# Revit family: Kälteschelle ALU-PU 80 -s-, DS 20, M10-M12, Ø108-133
name_source: partatom
category: HLS-Bauteile
revit_build: Autodesk Revit 2017 (Build: 20190507_1515(x64)
units: mm (PartAtom-declared; Revit-internal decimal feet)

## family parameters
Arbeitsebenenbasiert = Ja
Beim Laden mit Abzugskörper schneiden = Nein
Bemaßung runder Anschluss = Durchmesser verwenden
Gemeinsam genutzt = Ja
Immer vertikal = Nein
Raumberechnungspunkt = Nein
Teiletyp = Normal

## types (3) — shared parameters
A = 45 mm
Anschluss = M10/M12
BP = 14 mm  [stored 0.0459318 ft]
Baustoffklasse = B2
DS = 20 mm  [stored 0.0656168 ft]
DVS = 7 mm  [stored 0.0229659 ft]
Dichte Kern = 80 kg/m³
Dichte Mantel = 2.700 kg/m³
Dicke Mantel = 0,08 mm
Dämmkörper = ALU/PU
Dämmstärke = 20 mm  [stored 0.0656168 ft]
Fabrikat = MEFA
Firma = MEFA Befestigungs- und Montagesysteme GmbH
HGA = 22 mm  [stored 0.0721785 ft]
Kurztext1 = Kälteschelle RG80s ALU/PU
L Ü Bogen = 19 mm
MD = 3 mm  [stored 0.00984252 ft]
Material = Stahl
Material Mantel = Alufolie
Mengeneinheit = St
Oberflaeche = galvanisch verzinkt
Vorgabe-Ansicht = 1219 mm
Wasserdampfdiffusionswiderstand = 18750 µ
Wärmeleitfähigkeit = 0.025 W/mK
d1 = 7 mm  [stored 0.0229659 ft]
max. Temperaturbeständigkeit = 120 °C
mittl. Nenndruckfestigkeit Kern = 0,5 N/mm²
stat. Belastung Kern = 0,1 N/mm²
vpe = 1 St

## per-type parameters (varying)
- Kälteschelle ALU-PU 80 -s-, DS 20, M10/M12, Ø108: AB=0 mm  [stored 0 ft]; Anschlußhöhe=45 mm; Artikelnummer=75210850; B=196 mm; Breite=197 mm; D=108 mm; D0=148 mm; DF1=20 mm  [stored 0.0656168 ft]; DF2=20 mm  [stored 0.0656168 ft]; Dmax=110 mm; Dmin=108 mm; EAN=4250928443106; Gewicht=0.45 kg; Gewicht pro Bauteil=0.45 kg; H=176 mm; Kurztext2=108 mm Iso 20 x 83 mm M10/M12; L=83 mm  [stored 0.27231 ft]; MB=25 mm  [stored 0.082021 ft]; Materialname=DD11; R=74 mm; RM=77 mm; Rohraußendurchmesser Stahl=108 mm; Rohrschellentyp=Omnia MB; S=176 mm; S1=167 mm; Schalenlänge=83 mm; max. zul. Last=0.50 kN
- Kälteschelle ALU-PU 80 -s-, DS 20, M10/M12, Ø114,3: AB=0 mm  [stored 0 ft]; Anschlußhöhe=46 mm; Artikelnummer=75211442; B=206 mm  [stored 0.675853 ft]; Breite=234 mm; D=114 mm; D0=154 mm; DF1=22 mm  [stored 0.0721785 ft]; DF2=22 mm  [stored 0.0721785 ft]; Dmax=116 mm; Dmin=114 mm; EAN=4250928443120; Gewicht=0.62 kg; Gewicht pro Bauteil=0.62 kg; H=182 mm; Kurztext2=114,3 mm Iso 20 x 83 mm M10/M12; L=83 mm  [stored 0.27231 ft]; MB=30 mm  [stored 0.0984252 ft]; Materialname=S235; R=77 mm; RM=80 mm; Rohraußendurchmesser Stahl=114,3 mm; Rohrschellentyp=Maxima PSM; S=184 mm; S1=173 mm  [stored 0.567585 ft]; Schalenlänge=83 mm; max. zul. Last=0.70 kN
- Kälteschelle ALU-PU 80 -s-, DS 20, M10/M12, Ø133: AB=1 mm  [stored 0.00328084 ft]; Anschlußhöhe=46 mm; Artikelnummer=75613350; B=226 mm; Breite=225 mm; D=133 mm; D0=173 mm  [stored 0.567585 ft]; DF1=22 mm  [stored 0.0721785 ft]; DF2=22 mm  [stored 0.0721785 ft]; Dmax=136 mm; Dmin=132 mm; EAN=4250928443663; Gewicht=0.53 kg; Gewicht pro Bauteil=0.53 kg; H=201 mm; Kurztext2=133 mm Iso 20 x 100 mm M10/M12; L=100 mm  [stored 0.328084 ft]; MB=25 mm  [stored 0.082021 ft]; Materialname=DD11; R=87 mm; RM=90 mm; Rohraußendurchmesser Stahl=133 mm; Rohrschellentyp=Omnia MB; S=204 mm; S1=192 mm; Schalenlänge=100 mm; max. zul. Last=0.70 kN

note: [stored X ft] marks values corroborated as IEEE doubles in the binary element streams (Revit-internal decimal feet)

## geometry (parser evidence)
native form markers: Sweep x3
no freeform markers — native parametric forms only
